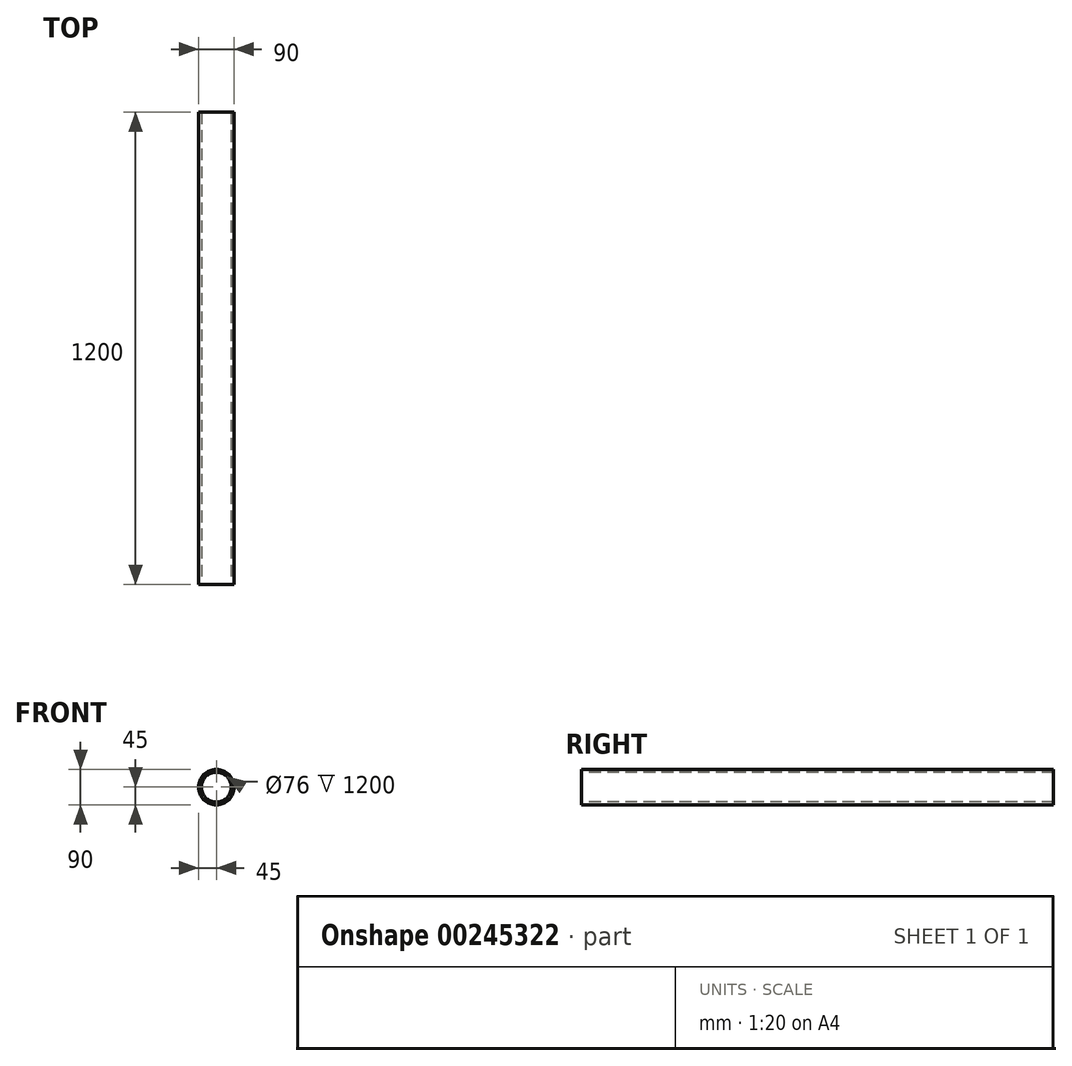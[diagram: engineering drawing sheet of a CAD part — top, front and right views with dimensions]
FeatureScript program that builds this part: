
annotation { "Feature Type Name" : "Feature", "Feature Type Description" : "" }
export const myFeature = defineFeature(function(context is Context, id is Id, definition is map)
    precondition{}
    {
        {
            var Q0;
            Q0=qCreatedBy(makeId("Front.planeOp"),FACE);
            var sketch = newSketch(context, id + "F0", { "sketchPlane" : qUnion([Q0])});
            skCircle(sketch, "E0", {"center": v(0, 0) * mm, "radius": 38 * mm});
            skCircle(sketch, "E1", {"center": v(0, 0) * mm, "radius": 45 * mm});
            skSolve(sketch);
        }
        {
            var Q0;
            Q0 = qSketchRegion(id + "F0", true);
            extrude(context, id + "F1", {"entities" : qUnion([Q0]), "oppositeDirection" : true, "depth" : 1200 * mm, "offsetDistance" : 25 * mm});
        }
    });
